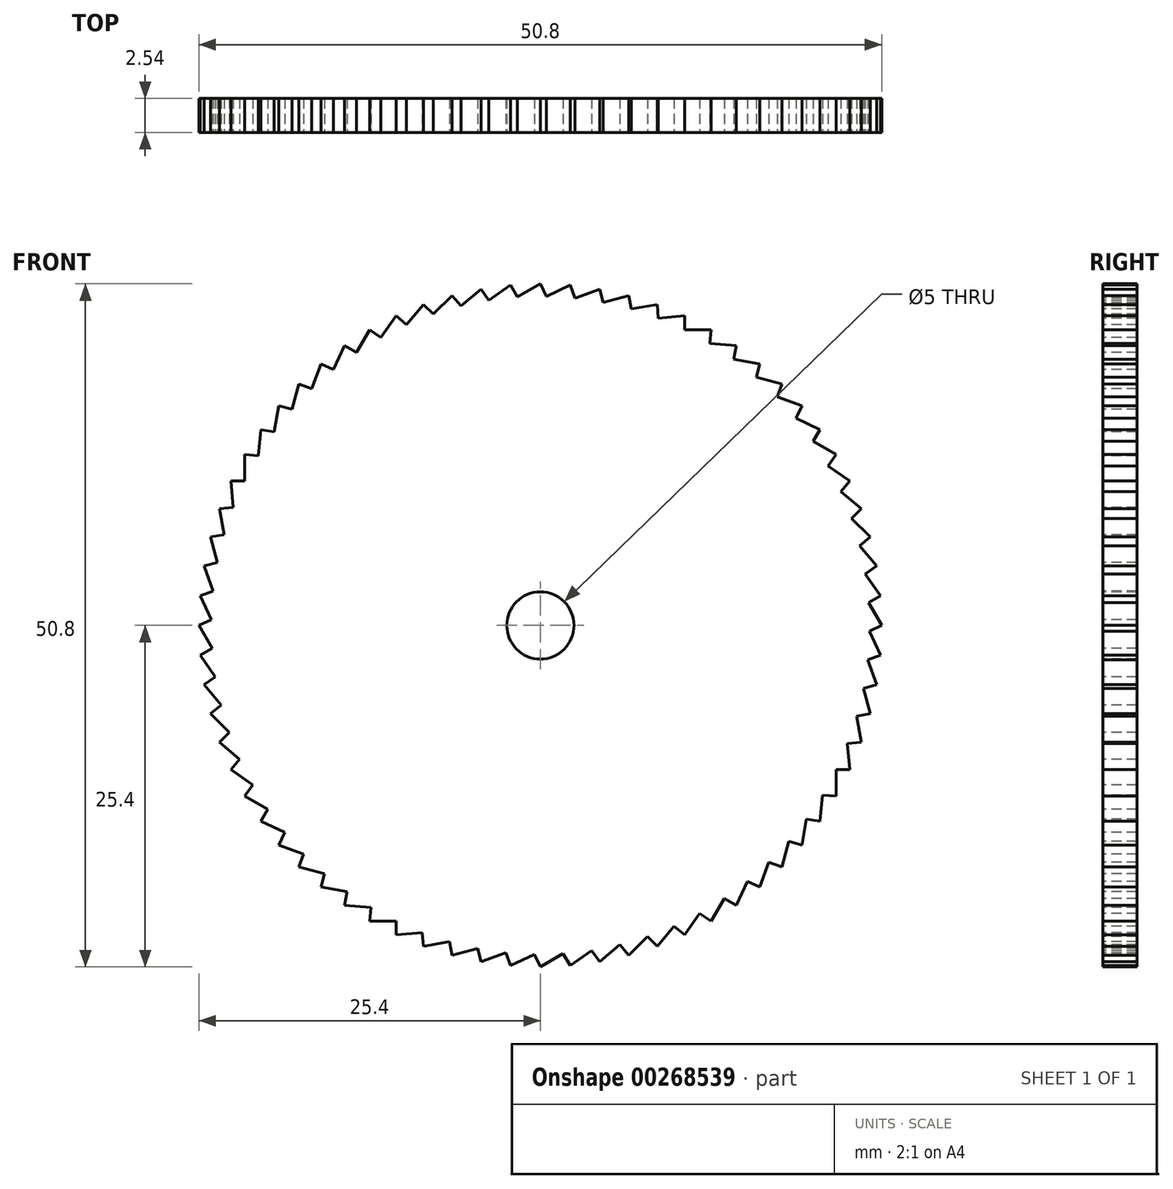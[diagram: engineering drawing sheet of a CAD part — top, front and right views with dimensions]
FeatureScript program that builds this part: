
annotation { "Feature Type Name" : "Feature", "Feature Type Description" : "" }
export const myFeature = defineFeature(function(context is Context, id is Id, definition is map)
    precondition{}
    {
        {
            var Q0;
            Q0=qCreatedBy(makeId("Front.planeOp"),FACE);
            var sketch = newSketch(context, id + "F0", { "sketchPlane" : qUnion([Q0])});
            skCircle(sketch, "E0", {"center": v(0, 0) * mm, "radius": 2.5 * mm});
            skCircle(sketch, "E1", {"center": v(0, 0) * mm, "radius": 25.4 * mm});
            skSolve(sketch);
        }
        {
            var Q0;
            Q0 = qSketchRegion(id + "F0", true);
            extrude(context, id + "F1", {"entities" : qUnion([Q0]), "oppositeDirection" : true, "offsetDistance" : 25.4 * mm, "depth" : 2.54 * mm});
        }
        {
            var Q0;
            Q0=makeQuery(id+"F1.opExtrude","CAP_FACE",FACE,{"disambiguationData":[OSD([sQuery(id+"F0.wireOp",EDGE,"E0"),sQuery(id+"F0.wireOp",EDGE,"E1")])],"isStart":true});
            var sketch = newSketch(context, id + "F2", { "sketchPlane" : qUnion([Q0])});
            skArc(sketch, "E2", {"start": v(2.21, 25.3) * mm, "mid": v(1.1, 25.38) * mm, "end": v(0, 25.4) * mm});
            skLineSegment(sketch, "E3", {"start": v(0, 25.4) * mm, "end": v(0.43, 24.47) * mm});
            skLineSegment(sketch, "E4", {"start": v(0.43, 24.47) * mm, "end": v(2.21, 25.3) * mm});
            skLineSegment(sketch, "E5", {"start": v(0, 0) * mm, "end": v(2.21, 25.3) * mm, "construction": true});
            skLineSegment(sketch, "E6.1.0", {"start": v(-2.21, 25.3) * mm, "end": v(-1.7, 24.42) * mm});
            skArc(sketch, "E6.1.1", {"start": v(0, 25.4) * mm, "mid": v(-1.1, 25.38) * mm, "end": v(-2.21, 25.3) * mm});
            skLineSegment(sketch, "E6.1.2", {"start": v(-1.7, 24.42) * mm, "end": v(0, 25.4) * mm});
            skLineSegment(sketch, "E6.2.0", {"start": v(-4.41, 25.01) * mm, "end": v(-3.82, 24.18) * mm});
            skArc(sketch, "E6.2.1", {"start": v(-2.21, 25.3) * mm, "mid": v(-3.32, 25.18) * mm, "end": v(-4.41, 25.01) * mm});
            skLineSegment(sketch, "E6.2.2", {"start": v(-3.82, 24.18) * mm, "end": v(-2.21, 25.3) * mm});
            skLineSegment(sketch, "E6.3.0", {"start": v(-6.57, 24.53) * mm, "end": v(-5.92, 23.75) * mm});
            skArc(sketch, "E6.3.1", {"start": v(-4.41, 25.01) * mm, "mid": v(-5.5, 24.8) * mm, "end": v(-6.57, 24.53) * mm});
            skLineSegment(sketch, "E6.3.2", {"start": v(-5.92, 23.75) * mm, "end": v(-4.41, 25.01) * mm});
            skLineSegment(sketch, "E6.4.0", {"start": v(-8.69, 23.87) * mm, "end": v(-7.96, 23.14) * mm});
            skArc(sketch, "E6.4.1", {"start": v(-6.57, 24.53) * mm, "mid": v(-7.64, 24.22) * mm, "end": v(-8.69, 23.87) * mm});
            skLineSegment(sketch, "E6.4.2", {"start": v(-7.96, 23.14) * mm, "end": v(-6.57, 24.53) * mm});
            skLineSegment(sketch, "E6.5.0", {"start": v(-10.73, 23.02) * mm, "end": v(-9.95, 22.36) * mm});
            skArc(sketch, "E6.5.1", {"start": v(-8.69, 23.87) * mm, "mid": v(-9.72, 23.47) * mm, "end": v(-10.73, 23.02) * mm});
            skLineSegment(sketch, "E6.5.2", {"start": v(-9.95, 22.36) * mm, "end": v(-8.69, 23.87) * mm});
            skLineSegment(sketch, "E6.6.0", {"start": v(-12.7, 22) * mm, "end": v(-11.86, 21.41) * mm});
            skArc(sketch, "E6.6.1", {"start": v(-10.73, 23.02) * mm, "mid": v(-11.73, 22.53) * mm, "end": v(-12.7, 22) * mm});
            skLineSegment(sketch, "E6.6.2", {"start": v(-11.86, 21.41) * mm, "end": v(-10.73, 23.02) * mm});
            skLineSegment(sketch, "E6.7.0", {"start": v(-14.57, 20.8) * mm, "end": v(-13.68, 20.3) * mm});
            skArc(sketch, "E6.7.1", {"start": v(-12.7, 22) * mm, "mid": v(-13.65, 21.42) * mm, "end": v(-14.57, 20.8) * mm});
            skLineSegment(sketch, "E6.7.2", {"start": v(-13.68, 20.3) * mm, "end": v(-12.7, 22) * mm});
            skLineSegment(sketch, "E7.2.8.0", {"start": v(-16.33, 19.46) * mm, "end": v(-15.4, 19.03) * mm});
            skArc(sketch, "E7.3.8.0", {"start": v(-14.57, 20.8) * mm, "mid": v(-15.46, 20.15) * mm, "end": v(-16.33, 19.46) * mm});
            skLineSegment(sketch, "E7.7.8.0", {"start": v(-15.4, 19.03) * mm, "end": v(-14.57, 20.8) * mm});
            skLineSegment(sketch, "E7.2.9.0", {"start": v(-17.96, 17.96) * mm, "end": v(-17, 17.61) * mm});
            skArc(sketch, "E7.3.9.0", {"start": v(-16.33, 19.46) * mm, "mid": v(-17.16, 18.73) * mm, "end": v(-17.96, 17.96) * mm});
            skLineSegment(sketch, "E7.7.9.0", {"start": v(-17, 17.61) * mm, "end": v(-16.33, 19.46) * mm});
            skLineSegment(sketch, "E7.2.10.0", {"start": v(-19.46, 16.33) * mm, "end": v(-18.47, 16.06) * mm});
            skArc(sketch, "E7.3.10.0", {"start": v(-17.96, 17.96) * mm, "mid": v(-18.73, 17.16) * mm, "end": v(-19.46, 16.33) * mm});
            skLineSegment(sketch, "E7.7.10.0", {"start": v(-18.47, 16.06) * mm, "end": v(-17.96, 17.96) * mm});
            skLineSegment(sketch, "E7.2.11.0", {"start": v(-20.8, 14.57) * mm, "end": v(-19.8, 14.4) * mm});
            skArc(sketch, "E7.3.11.0", {"start": v(-19.46, 16.33) * mm, "mid": v(-20.15, 15.46) * mm, "end": v(-20.8, 14.57) * mm});
            skLineSegment(sketch, "E7.7.11.0", {"start": v(-19.8, 14.4) * mm, "end": v(-19.46, 16.33) * mm});
            skLineSegment(sketch, "E7.2.12.0", {"start": v(-22, 12.7) * mm, "end": v(-20.98, 12.61) * mm});
            skArc(sketch, "E7.3.12.0", {"start": v(-20.8, 14.57) * mm, "mid": v(-21.42, 13.65) * mm, "end": v(-22, 12.7) * mm});
            skLineSegment(sketch, "E7.7.12.0", {"start": v(-20.98, 12.61) * mm, "end": v(-20.8, 14.57) * mm});
            skLineSegment(sketch, "E7.2.13.0", {"start": v(-23.02, 10.73) * mm, "end": v(-22, 10.73) * mm});
            skArc(sketch, "E7.3.13.0", {"start": v(-22, 12.7) * mm, "mid": v(-22.53, 11.73) * mm, "end": v(-23.02, 10.73) * mm});
            skLineSegment(sketch, "E7.7.13.0", {"start": v(-22, 10.73) * mm, "end": v(-22, 12.7) * mm});
            skLineSegment(sketch, "E7.2.14.0", {"start": v(-23.87, 8.69) * mm, "end": v(-22.85, 8.78) * mm});
            skArc(sketch, "E7.3.14.0", {"start": v(-23.02, 10.73) * mm, "mid": v(-23.47, 9.72) * mm, "end": v(-23.87, 8.69) * mm});
            skLineSegment(sketch, "E7.7.14.0", {"start": v(-22.85, 8.78) * mm, "end": v(-23.02, 10.73) * mm});
            skLineSegment(sketch, "E7.2.15.0", {"start": v(-24.53, 6.57) * mm, "end": v(-23.53, 6.75) * mm});
            skArc(sketch, "E7.3.15.0", {"start": v(-23.87, 8.69) * mm, "mid": v(-24.22, 7.64) * mm, "end": v(-24.53, 6.57) * mm});
            skLineSegment(sketch, "E7.7.15.0", {"start": v(-23.53, 6.75) * mm, "end": v(-23.87, 8.69) * mm});
            skLineSegment(sketch, "E8.2.16.0", {"start": v(-25.01, 4.41) * mm, "end": v(-24.03, 4.68) * mm});
            skArc(sketch, "E8.3.16.0", {"start": v(-24.53, 6.57) * mm, "mid": v(-24.8, 5.5) * mm, "end": v(-25.01, 4.41) * mm});
            skLineSegment(sketch, "E8.7.16.0", {"start": v(-24.03, 4.68) * mm, "end": v(-24.53, 6.57) * mm});
            skLineSegment(sketch, "E8.2.17.0", {"start": v(-25.3, 2.21) * mm, "end": v(-24.34, 2.56) * mm});
            skArc(sketch, "E8.3.17.0", {"start": v(-25.01, 4.41) * mm, "mid": v(-25.18, 3.32) * mm, "end": v(-25.3, 2.21) * mm});
            skLineSegment(sketch, "E8.7.17.0", {"start": v(-24.34, 2.56) * mm, "end": v(-25.01, 4.41) * mm});
            skLineSegment(sketch, "E8.2.18.0", {"start": v(-25.4, 0) * mm, "end": v(-24.47, 0.43) * mm});
            skArc(sketch, "E8.3.18.0", {"start": v(-25.3, 2.21) * mm, "mid": v(-25.38, 1.1) * mm, "end": v(-25.4, 0) * mm});
            skLineSegment(sketch, "E8.7.18.0", {"start": v(-24.47, 0.43) * mm, "end": v(-25.3, 2.21) * mm});
            skLineSegment(sketch, "E8.2.19.0", {"start": v(-25.3, -2.21) * mm, "end": v(-24.42, -1.7) * mm});
            skArc(sketch, "E8.3.19.0", {"start": v(-25.4, 0) * mm, "mid": v(-25.38, -1.1) * mm, "end": v(-25.3, -2.21) * mm});
            skLineSegment(sketch, "E8.7.19.0", {"start": v(-24.42, -1.7) * mm, "end": v(-25.4, 0) * mm});
            skLineSegment(sketch, "E8.2.20.0", {"start": v(-25.01, -4.41) * mm, "end": v(-24.18, -3.82) * mm});
            skArc(sketch, "E8.3.20.0", {"start": v(-25.3, -2.21) * mm, "mid": v(-25.18, -3.32) * mm, "end": v(-25.01, -4.41) * mm});
            skLineSegment(sketch, "E8.7.20.0", {"start": v(-24.18, -3.82) * mm, "end": v(-25.3, -2.21) * mm});
            skLineSegment(sketch, "E8.2.21.0", {"start": v(-24.53, -6.57) * mm, "end": v(-23.75, -5.92) * mm});
            skArc(sketch, "E8.3.21.0", {"start": v(-25.01, -4.41) * mm, "mid": v(-24.8, -5.5) * mm, "end": v(-24.53, -6.57) * mm});
            skLineSegment(sketch, "E8.7.21.0", {"start": v(-23.75, -5.92) * mm, "end": v(-25.01, -4.41) * mm});
            skLineSegment(sketch, "E8.2.22.0", {"start": v(-23.87, -8.69) * mm, "end": v(-23.14, -7.96) * mm});
            skArc(sketch, "E8.3.22.0", {"start": v(-24.53, -6.57) * mm, "mid": v(-24.22, -7.64) * mm, "end": v(-23.87, -8.69) * mm});
            skLineSegment(sketch, "E8.7.22.0", {"start": v(-23.14, -7.96) * mm, "end": v(-24.53, -6.57) * mm});
            skLineSegment(sketch, "E8.2.23.0", {"start": v(-23.02, -10.73) * mm, "end": v(-22.36, -9.95) * mm});
            skArc(sketch, "E8.3.23.0", {"start": v(-23.87, -8.69) * mm, "mid": v(-23.47, -9.72) * mm, "end": v(-23.02, -10.73) * mm});
            skLineSegment(sketch, "E8.7.23.0", {"start": v(-22.36, -9.95) * mm, "end": v(-23.87, -8.69) * mm});
            skLineSegment(sketch, "E9", {"start": v(0, 25.4) * mm, "end": v(0, 0) * mm, "construction": true});
            skLineSegment(sketch, "E10.2.24.0", {"start": v(-22, -12.7) * mm, "end": v(-21.41, -11.86) * mm});
            skArc(sketch, "E10.3.24.0", {"start": v(-23.02, -10.73) * mm, "mid": v(-22.53, -11.73) * mm, "end": v(-22, -12.7) * mm});
            skLineSegment(sketch, "E10.7.24.0", {"start": v(-21.41, -11.86) * mm, "end": v(-23.02, -10.73) * mm});
            skLineSegment(sketch, "E10.2.25.0", {"start": v(-20.8, -14.57) * mm, "end": v(-20.3, -13.68) * mm});
            skArc(sketch, "E10.3.25.0", {"start": v(-22, -12.7) * mm, "mid": v(-21.42, -13.65) * mm, "end": v(-20.8, -14.57) * mm});
            skLineSegment(sketch, "E10.7.25.0", {"start": v(-20.3, -13.68) * mm, "end": v(-22, -12.7) * mm});
            skLineSegment(sketch, "E10.2.26.0", {"start": v(-19.46, -16.33) * mm, "end": v(-19.03, -15.4) * mm});
            skArc(sketch, "E10.3.26.0", {"start": v(-20.8, -14.57) * mm, "mid": v(-20.15, -15.46) * mm, "end": v(-19.46, -16.33) * mm});
            skLineSegment(sketch, "E10.7.26.0", {"start": v(-19.03, -15.4) * mm, "end": v(-20.8, -14.57) * mm});
            skLineSegment(sketch, "E10.2.27.0", {"start": v(-17.96, -17.96) * mm, "end": v(-17.61, -17) * mm});
            skArc(sketch, "E10.3.27.0", {"start": v(-19.46, -16.33) * mm, "mid": v(-18.73, -17.16) * mm, "end": v(-17.96, -17.96) * mm});
            skLineSegment(sketch, "E10.7.27.0", {"start": v(-17.61, -17) * mm, "end": v(-19.46, -16.33) * mm});
            skLineSegment(sketch, "E10.2.28.0", {"start": v(-16.33, -19.46) * mm, "end": v(-16.06, -18.47) * mm});
            skArc(sketch, "E10.3.28.0", {"start": v(-17.96, -17.96) * mm, "mid": v(-17.16, -18.73) * mm, "end": v(-16.33, -19.46) * mm});
            skLineSegment(sketch, "E10.7.28.0", {"start": v(-16.06, -18.47) * mm, "end": v(-17.96, -17.96) * mm});
            skLineSegment(sketch, "E10.2.29.0", {"start": v(-14.57, -20.8) * mm, "end": v(-14.4, -19.8) * mm});
            skArc(sketch, "E10.3.29.0", {"start": v(-16.33, -19.46) * mm, "mid": v(-15.46, -20.15) * mm, "end": v(-14.57, -20.8) * mm});
            skLineSegment(sketch, "E10.7.29.0", {"start": v(-14.4, -19.8) * mm, "end": v(-16.33, -19.46) * mm});
            skLineSegment(sketch, "E10.2.30.0", {"start": v(-12.7, -22) * mm, "end": v(-12.61, -20.98) * mm});
            skArc(sketch, "E10.3.30.0", {"start": v(-14.57, -20.8) * mm, "mid": v(-13.65, -21.42) * mm, "end": v(-12.7, -22) * mm});
            skLineSegment(sketch, "E10.7.30.0", {"start": v(-12.61, -20.98) * mm, "end": v(-14.57, -20.8) * mm});
            skLineSegment(sketch, "E10.2.31.0", {"start": v(-10.73, -23.02) * mm, "end": v(-10.73, -22) * mm});
            skArc(sketch, "E10.3.31.0", {"start": v(-12.7, -22) * mm, "mid": v(-11.73, -22.53) * mm, "end": v(-10.73, -23.02) * mm});
            skLineSegment(sketch, "E10.7.31.0", {"start": v(-10.73, -22) * mm, "end": v(-12.7, -22) * mm});
            skLineSegment(sketch, "E10.2.32.0", {"start": v(-8.69, -23.87) * mm, "end": v(-8.78, -22.85) * mm});
            skArc(sketch, "E10.3.32.0", {"start": v(-10.73, -23.02) * mm, "mid": v(-9.72, -23.47) * mm, "end": v(-8.69, -23.87) * mm});
            skLineSegment(sketch, "E10.7.32.0", {"start": v(-8.78, -22.85) * mm, "end": v(-10.73, -23.02) * mm});
            skLineSegment(sketch, "E10.2.33.0", {"start": v(-6.57, -24.53) * mm, "end": v(-6.75, -23.53) * mm});
            skArc(sketch, "E10.3.33.0", {"start": v(-8.69, -23.87) * mm, "mid": v(-7.64, -24.22) * mm, "end": v(-6.57, -24.53) * mm});
            skLineSegment(sketch, "E10.7.33.0", {"start": v(-6.75, -23.53) * mm, "end": v(-8.69, -23.87) * mm});
            skLineSegment(sketch, "E10.2.34.0", {"start": v(-4.41, -25.01) * mm, "end": v(-4.68, -24.03) * mm});
            skArc(sketch, "E10.3.34.0", {"start": v(-6.57, -24.53) * mm, "mid": v(-5.5, -24.8) * mm, "end": v(-4.41, -25.01) * mm});
            skLineSegment(sketch, "E10.7.34.0", {"start": v(-4.68, -24.03) * mm, "end": v(-6.57, -24.53) * mm});
            skLineSegment(sketch, "E10.2.35.0", {"start": v(-2.21, -25.3) * mm, "end": v(-2.56, -24.34) * mm});
            skArc(sketch, "E10.3.35.0", {"start": v(-4.41, -25.01) * mm, "mid": v(-3.32, -25.18) * mm, "end": v(-2.21, -25.3) * mm});
            skLineSegment(sketch, "E10.7.35.0", {"start": v(-2.56, -24.34) * mm, "end": v(-4.41, -25.01) * mm});
            skLineSegment(sketch, "E10.2.36.0", {"start": v(0, -25.4) * mm, "end": v(-0.43, -24.47) * mm});
            skArc(sketch, "E10.3.36.0", {"start": v(-2.21, -25.3) * mm, "mid": v(-1.1, -25.38) * mm, "end": v(0, -25.4) * mm});
            skLineSegment(sketch, "E10.7.36.0", {"start": v(-0.43, -24.47) * mm, "end": v(-2.21, -25.3) * mm});
            skLineSegment(sketch, "E10.2.37.0", {"start": v(2.21, -25.3) * mm, "end": v(1.7, -24.42) * mm});
            skArc(sketch, "E10.3.37.0", {"start": v(0, -25.4) * mm, "mid": v(1.1, -25.38) * mm, "end": v(2.21, -25.3) * mm});
            skLineSegment(sketch, "E10.7.37.0", {"start": v(1.7, -24.42) * mm, "end": v(0, -25.4) * mm});
            skLineSegment(sketch, "E10.2.38.0", {"start": v(4.41, -25.01) * mm, "end": v(3.82, -24.18) * mm});
            skArc(sketch, "E10.3.38.0", {"start": v(2.21, -25.3) * mm, "mid": v(3.32, -25.18) * mm, "end": v(4.41, -25.01) * mm});
            skLineSegment(sketch, "E10.7.38.0", {"start": v(3.82, -24.18) * mm, "end": v(2.21, -25.3) * mm});
            skLineSegment(sketch, "E10.2.39.0", {"start": v(6.57, -24.53) * mm, "end": v(5.92, -23.75) * mm});
            skArc(sketch, "E10.3.39.0", {"start": v(4.41, -25.01) * mm, "mid": v(5.5, -24.8) * mm, "end": v(6.57, -24.53) * mm});
            skLineSegment(sketch, "E10.7.39.0", {"start": v(5.92, -23.75) * mm, "end": v(4.41, -25.01) * mm});
            skLineSegment(sketch, "E10.2.40.0", {"start": v(8.69, -23.87) * mm, "end": v(7.96, -23.14) * mm});
            skArc(sketch, "E10.3.40.0", {"start": v(6.57, -24.53) * mm, "mid": v(7.64, -24.22) * mm, "end": v(8.69, -23.87) * mm});
            skLineSegment(sketch, "E10.7.40.0", {"start": v(7.96, -23.14) * mm, "end": v(6.57, -24.53) * mm});
            skLineSegment(sketch, "E10.2.41.0", {"start": v(10.73, -23.02) * mm, "end": v(9.95, -22.36) * mm});
            skArc(sketch, "E10.3.41.0", {"start": v(8.69, -23.87) * mm, "mid": v(9.72, -23.47) * mm, "end": v(10.73, -23.02) * mm});
            skLineSegment(sketch, "E10.7.41.0", {"start": v(9.95, -22.36) * mm, "end": v(8.69, -23.87) * mm});
            skLineSegment(sketch, "E10.2.42.0", {"start": v(12.7, -22) * mm, "end": v(11.86, -21.41) * mm});
            skArc(sketch, "E10.3.42.0", {"start": v(10.73, -23.02) * mm, "mid": v(11.73, -22.53) * mm, "end": v(12.7, -22) * mm});
            skLineSegment(sketch, "E10.7.42.0", {"start": v(11.86, -21.41) * mm, "end": v(10.73, -23.02) * mm});
            skLineSegment(sketch, "E10.2.43.0", {"start": v(14.57, -20.8) * mm, "end": v(13.68, -20.3) * mm});
            skArc(sketch, "E10.3.43.0", {"start": v(12.7, -22) * mm, "mid": v(13.65, -21.42) * mm, "end": v(14.57, -20.8) * mm});
            skLineSegment(sketch, "E10.7.43.0", {"start": v(13.68, -20.3) * mm, "end": v(12.7, -22) * mm});
            skLineSegment(sketch, "E10.2.44.0", {"start": v(16.33, -19.46) * mm, "end": v(15.4, -19.03) * mm});
            skArc(sketch, "E10.3.44.0", {"start": v(14.57, -20.8) * mm, "mid": v(15.46, -20.15) * mm, "end": v(16.33, -19.46) * mm});
            skLineSegment(sketch, "E10.7.44.0", {"start": v(15.4, -19.03) * mm, "end": v(14.57, -20.8) * mm});
            skLineSegment(sketch, "E10.2.45.0", {"start": v(17.96, -17.96) * mm, "end": v(17, -17.61) * mm});
            skArc(sketch, "E10.3.45.0", {"start": v(16.33, -19.46) * mm, "mid": v(17.16, -18.73) * mm, "end": v(17.96, -17.96) * mm});
            skLineSegment(sketch, "E10.7.45.0", {"start": v(17, -17.61) * mm, "end": v(16.33, -19.46) * mm});
            skLineSegment(sketch, "E10.2.46.0", {"start": v(19.46, -16.33) * mm, "end": v(18.47, -16.06) * mm});
            skArc(sketch, "E10.3.46.0", {"start": v(17.96, -17.96) * mm, "mid": v(18.73, -17.16) * mm, "end": v(19.46, -16.33) * mm});
            skLineSegment(sketch, "E10.7.46.0", {"start": v(18.47, -16.06) * mm, "end": v(17.96, -17.96) * mm});
            skLineSegment(sketch, "E10.2.47.0", {"start": v(20.8, -14.57) * mm, "end": v(19.8, -14.4) * mm});
            skArc(sketch, "E10.3.47.0", {"start": v(19.46, -16.33) * mm, "mid": v(20.15, -15.46) * mm, "end": v(20.8, -14.57) * mm});
            skLineSegment(sketch, "E10.7.47.0", {"start": v(19.8, -14.4) * mm, "end": v(19.46, -16.33) * mm});
            skLineSegment(sketch, "E11.2.48.0", {"start": v(22, -12.7) * mm, "end": v(20.98, -12.61) * mm});
            skArc(sketch, "E11.3.48.0", {"start": v(20.8, -14.57) * mm, "mid": v(21.42, -13.65) * mm, "end": v(22, -12.7) * mm});
            skLineSegment(sketch, "E11.7.48.0", {"start": v(20.98, -12.61) * mm, "end": v(20.8, -14.57) * mm});
            skLineSegment(sketch, "E11.2.49.0", {"start": v(23.02, -10.73) * mm, "end": v(22, -10.73) * mm});
            skArc(sketch, "E11.3.49.0", {"start": v(22, -12.7) * mm, "mid": v(22.53, -11.73) * mm, "end": v(23.02, -10.73) * mm});
            skLineSegment(sketch, "E11.7.49.0", {"start": v(22, -10.73) * mm, "end": v(22, -12.7) * mm});
            skLineSegment(sketch, "E11.2.50.0", {"start": v(23.87, -8.69) * mm, "end": v(22.85, -8.78) * mm});
            skArc(sketch, "E11.3.50.0", {"start": v(23.02, -10.73) * mm, "mid": v(23.47, -9.72) * mm, "end": v(23.87, -8.69) * mm});
            skLineSegment(sketch, "E11.7.50.0", {"start": v(22.85, -8.78) * mm, "end": v(23.02, -10.73) * mm});
            skLineSegment(sketch, "E11.2.51.0", {"start": v(24.53, -6.57) * mm, "end": v(23.53, -6.75) * mm});
            skArc(sketch, "E11.3.51.0", {"start": v(23.87, -8.69) * mm, "mid": v(24.22, -7.64) * mm, "end": v(24.53, -6.57) * mm});
            skLineSegment(sketch, "E11.7.51.0", {"start": v(23.53, -6.75) * mm, "end": v(23.87, -8.69) * mm});
            skLineSegment(sketch, "E11.2.52.0", {"start": v(25.01, -4.41) * mm, "end": v(24.03, -4.68) * mm});
            skArc(sketch, "E11.3.52.0", {"start": v(24.53, -6.57) * mm, "mid": v(24.8, -5.5) * mm, "end": v(25.01, -4.41) * mm});
            skLineSegment(sketch, "E11.7.52.0", {"start": v(24.03, -4.68) * mm, "end": v(24.53, -6.57) * mm});
            skLineSegment(sketch, "E11.2.53.0", {"start": v(25.3, -2.21) * mm, "end": v(24.34, -2.56) * mm});
            skArc(sketch, "E11.3.53.0", {"start": v(25.01, -4.41) * mm, "mid": v(25.18, -3.32) * mm, "end": v(25.3, -2.21) * mm});
            skLineSegment(sketch, "E11.7.53.0", {"start": v(24.34, -2.56) * mm, "end": v(25.01, -4.41) * mm});
            skLineSegment(sketch, "E11.2.54.0", {"start": v(25.4, 0) * mm, "end": v(24.47, -0.43) * mm});
            skArc(sketch, "E11.3.54.0", {"start": v(25.3, -2.21) * mm, "mid": v(25.38, -1.1) * mm, "end": v(25.4, 0) * mm});
            skLineSegment(sketch, "E11.7.54.0", {"start": v(24.47, -0.43) * mm, "end": v(25.3, -2.21) * mm});
            skLineSegment(sketch, "E11.2.55.0", {"start": v(25.3, 2.21) * mm, "end": v(24.42, 1.7) * mm});
            skArc(sketch, "E11.3.55.0", {"start": v(25.4, 0) * mm, "mid": v(25.38, 1.1) * mm, "end": v(25.3, 2.21) * mm});
            skLineSegment(sketch, "E11.7.55.0", {"start": v(24.42, 1.7) * mm, "end": v(25.4, 0) * mm});
            skLineSegment(sketch, "E11.2.56.0", {"start": v(25.01, 4.41) * mm, "end": v(24.18, 3.82) * mm});
            skArc(sketch, "E11.3.56.0", {"start": v(25.3, 2.21) * mm, "mid": v(25.18, 3.32) * mm, "end": v(25.01, 4.41) * mm});
            skLineSegment(sketch, "E11.7.56.0", {"start": v(24.18, 3.82) * mm, "end": v(25.3, 2.21) * mm});
            skLineSegment(sketch, "E11.2.57.0", {"start": v(24.53, 6.57) * mm, "end": v(23.75, 5.92) * mm});
            skArc(sketch, "E11.3.57.0", {"start": v(25.01, 4.41) * mm, "mid": v(24.8, 5.5) * mm, "end": v(24.53, 6.57) * mm});
            skLineSegment(sketch, "E11.7.57.0", {"start": v(23.75, 5.92) * mm, "end": v(25.01, 4.41) * mm});
            skLineSegment(sketch, "E11.2.58.0", {"start": v(23.87, 8.69) * mm, "end": v(23.14, 7.96) * mm});
            skArc(sketch, "E11.3.58.0", {"start": v(24.53, 6.57) * mm, "mid": v(24.22, 7.64) * mm, "end": v(23.87, 8.69) * mm});
            skLineSegment(sketch, "E11.7.58.0", {"start": v(23.14, 7.96) * mm, "end": v(24.53, 6.57) * mm});
            skLineSegment(sketch, "E11.2.59.0", {"start": v(23.02, 10.73) * mm, "end": v(22.36, 9.95) * mm});
            skArc(sketch, "E11.3.59.0", {"start": v(23.87, 8.69) * mm, "mid": v(23.47, 9.72) * mm, "end": v(23.02, 10.73) * mm});
            skLineSegment(sketch, "E11.7.59.0", {"start": v(22.36, 9.95) * mm, "end": v(23.87, 8.69) * mm});
            skLineSegment(sketch, "E11.2.60.0", {"start": v(22, 12.7) * mm, "end": v(21.41, 11.86) * mm});
            skArc(sketch, "E11.3.60.0", {"start": v(23.02, 10.73) * mm, "mid": v(22.53, 11.73) * mm, "end": v(22, 12.7) * mm});
            skLineSegment(sketch, "E11.7.60.0", {"start": v(21.41, 11.86) * mm, "end": v(23.02, 10.73) * mm});
            skLineSegment(sketch, "E11.2.61.0", {"start": v(20.8, 14.57) * mm, "end": v(20.3, 13.68) * mm});
            skArc(sketch, "E11.3.61.0", {"start": v(22, 12.7) * mm, "mid": v(21.42, 13.65) * mm, "end": v(20.8, 14.57) * mm});
            skLineSegment(sketch, "E11.7.61.0", {"start": v(20.3, 13.68) * mm, "end": v(22, 12.7) * mm});
            skLineSegment(sketch, "E11.2.62.0", {"start": v(19.46, 16.33) * mm, "end": v(19.03, 15.4) * mm});
            skArc(sketch, "E11.3.62.0", {"start": v(20.8, 14.57) * mm, "mid": v(20.15, 15.46) * mm, "end": v(19.46, 16.33) * mm});
            skLineSegment(sketch, "E11.7.62.0", {"start": v(19.03, 15.4) * mm, "end": v(20.8, 14.57) * mm});
            skLineSegment(sketch, "E11.2.63.0", {"start": v(17.96, 17.96) * mm, "end": v(17.61, 17) * mm});
            skArc(sketch, "E11.3.63.0", {"start": v(19.46, 16.33) * mm, "mid": v(18.73, 17.16) * mm, "end": v(17.96, 17.96) * mm});
            skLineSegment(sketch, "E11.7.63.0", {"start": v(17.61, 17) * mm, "end": v(19.46, 16.33) * mm});
            skLineSegment(sketch, "E11.2.64.0", {"start": v(16.33, 19.46) * mm, "end": v(16.06, 18.47) * mm});
            skArc(sketch, "E11.3.64.0", {"start": v(17.96, 17.96) * mm, "mid": v(17.16, 18.73) * mm, "end": v(16.33, 19.46) * mm});
            skLineSegment(sketch, "E11.7.64.0", {"start": v(16.06, 18.47) * mm, "end": v(17.96, 17.96) * mm});
            skLineSegment(sketch, "E11.2.65.0", {"start": v(14.57, 20.8) * mm, "end": v(14.4, 19.8) * mm});
            skArc(sketch, "E11.3.65.0", {"start": v(16.33, 19.46) * mm, "mid": v(15.46, 20.15) * mm, "end": v(14.57, 20.8) * mm});
            skLineSegment(sketch, "E11.7.65.0", {"start": v(14.4, 19.8) * mm, "end": v(16.33, 19.46) * mm});
            skLineSegment(sketch, "E11.2.66.0", {"start": v(12.7, 22) * mm, "end": v(12.61, 20.98) * mm});
            skArc(sketch, "E11.3.66.0", {"start": v(14.57, 20.8) * mm, "mid": v(13.65, 21.42) * mm, "end": v(12.7, 22) * mm});
            skLineSegment(sketch, "E11.7.66.0", {"start": v(12.61, 20.98) * mm, "end": v(14.57, 20.8) * mm});
            skLineSegment(sketch, "E11.2.67.0", {"start": v(10.73, 23.02) * mm, "end": v(10.73, 22) * mm});
            skArc(sketch, "E11.3.67.0", {"start": v(12.7, 22) * mm, "mid": v(11.73, 22.53) * mm, "end": v(10.73, 23.02) * mm});
            skLineSegment(sketch, "E11.7.67.0", {"start": v(10.73, 22) * mm, "end": v(12.7, 22) * mm});
            skLineSegment(sketch, "E11.2.68.0", {"start": v(8.69, 23.87) * mm, "end": v(8.78, 22.85) * mm});
            skArc(sketch, "E11.3.68.0", {"start": v(10.73, 23.02) * mm, "mid": v(9.72, 23.47) * mm, "end": v(8.69, 23.87) * mm});
            skLineSegment(sketch, "E11.7.68.0", {"start": v(8.78, 22.85) * mm, "end": v(10.73, 23.02) * mm});
            skLineSegment(sketch, "E11.2.69.0", {"start": v(6.57, 24.53) * mm, "end": v(6.75, 23.53) * mm});
            skArc(sketch, "E11.3.69.0", {"start": v(8.69, 23.87) * mm, "mid": v(7.64, 24.22) * mm, "end": v(6.57, 24.53) * mm});
            skLineSegment(sketch, "E11.7.69.0", {"start": v(6.75, 23.53) * mm, "end": v(8.69, 23.87) * mm});
            skLineSegment(sketch, "E11.2.70.0", {"start": v(4.41, 25.01) * mm, "end": v(4.68, 24.03) * mm});
            skArc(sketch, "E11.3.70.0", {"start": v(6.57, 24.53) * mm, "mid": v(5.5, 24.8) * mm, "end": v(4.41, 25.01) * mm});
            skLineSegment(sketch, "E11.7.70.0", {"start": v(4.68, 24.03) * mm, "end": v(6.57, 24.53) * mm});
            skLineSegment(sketch, "E11.2.71.0", {"start": v(2.21, 25.3) * mm, "end": v(2.56, 24.34) * mm});
            skArc(sketch, "E11.3.71.0", {"start": v(4.41, 25.01) * mm, "mid": v(3.32, 25.18) * mm, "end": v(2.21, 25.3) * mm});
            skLineSegment(sketch, "E11.7.71.0", {"start": v(2.56, 24.34) * mm, "end": v(4.41, 25.01) * mm});
            skSolve(sketch);
        }
        {
            var Q0;
            Q0 = qSketchRegion(id + "F2", true);
            extrude(context, id + "F3", {"entities" : qUnion([Q0]), "operationType" : NewBodyOperationType.REMOVE, "oppositeDirection" : true, "offsetDistance" : 25.4 * mm, "depth" : 25.4 * mm});
        }
    });
